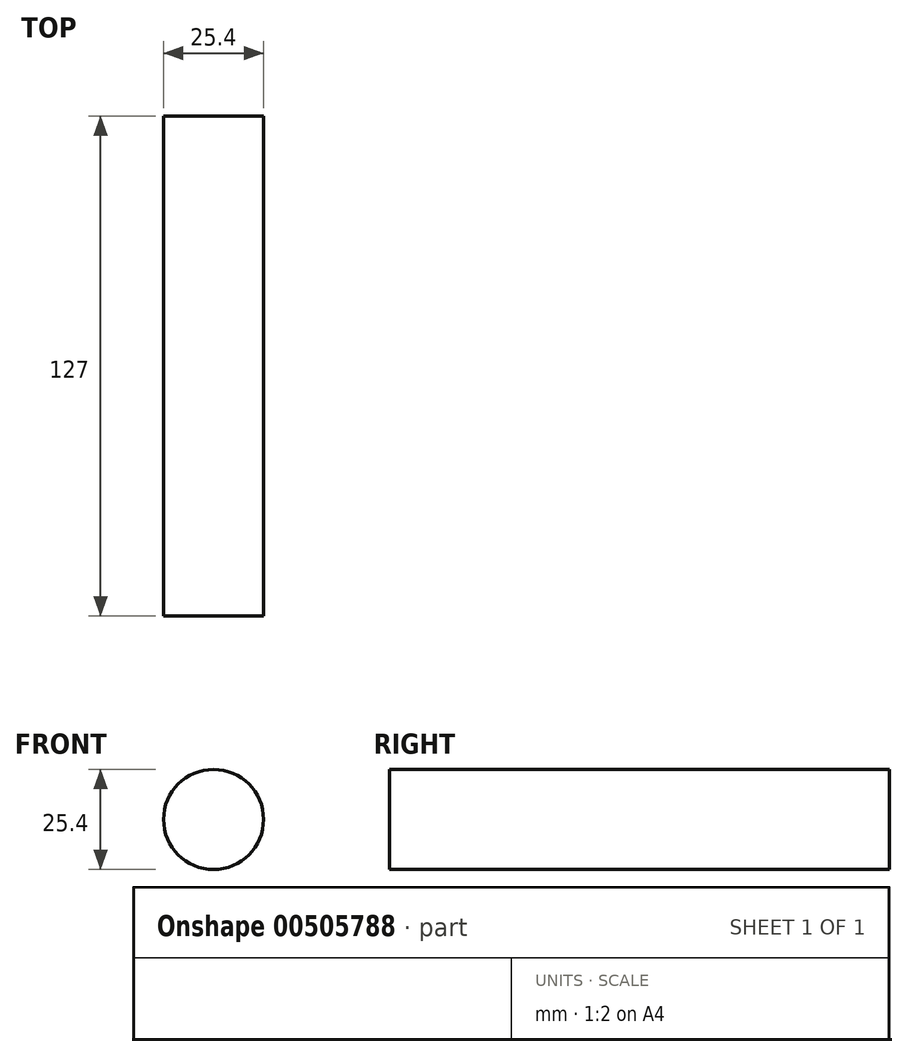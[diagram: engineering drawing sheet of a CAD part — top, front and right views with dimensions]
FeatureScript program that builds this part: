
annotation { "Feature Type Name" : "Feature", "Feature Type Description" : "" }
export const myFeature = defineFeature(function(context is Context, id is Id, definition is map)
    precondition{}
    {
        {
            var Q0;
            Q0=qCreatedBy(makeId("Front.planeOp"),FACE);
            var sketch = newSketch(context, id + "F0", { "sketchPlane" : qUnion([Q0])});
            skCircle(sketch, "E0", {"center": v(0, 0) * mm, "radius": 12.7 * mm});
            skSolve(sketch);
        }
        {
            var Q0;
            Q0=makeQuery(id+"F0.imprint","IMPRINT",FACE,{"disambiguationData":[TD([[makeQuery(id+"F0.imprint","IMPRINT",EDGE,{"derivedFrom":sQuery(id+"F0.wireOp",EDGE,"E0")}),1.0]])]});
            extrude(context, id + "F1", {"entities" : qUnion([Q0]), "depth" : 127 * mm, "offsetDistance" : 25.4 * mm});
        }
    });
